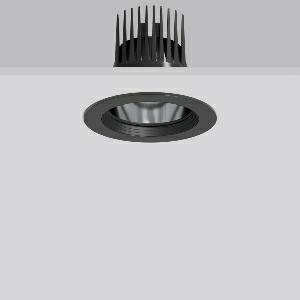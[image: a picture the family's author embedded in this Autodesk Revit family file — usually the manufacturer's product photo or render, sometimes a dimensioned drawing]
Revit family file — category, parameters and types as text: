
# Revit family: heledon_maxi_e_901756_003_1_76_3207
name_source: partatom
category: Lighting Fixtures
units: mm (PartAtom-declared; Revit-internal decimal feet)

## family parameters
Cut with Voids When Loaded = No
Host = Face
Light Source = No
Part Type = Normal
Room Calculation Point = No
Round Connector Dimension = Use Diameter
Shared = No

## types (1)
- HELEDON maxi E (1 x LED Modul 940, 3400 lm, 4000)
    Apparent Load = 25 VA
    Approval mark = CE
    CIE Flux Codes = 100 100 100 100 100
    Color Rendering = 92
    Color Temperature = 4000
    Default Elevation = 1800 mm
    Description = Series: HELEDON maxi
Round recessed downlight. Housing: die-cast aluminium, powder-coated. Black plastic ring and recessed LED to prevent glare from the side. Optical assembly with reflector made of MIRO-Silver with 98% total light reflection for outstanding efficiency - can be changed without tools. Best colour rendering index Ra>90. Suitable for Recessed ceiling mounting. Installation without tools thanks to spring fastening system. Including separate LED converter with connecting cable 600 mm.High quality converter without flickering and stroboscopic effect. Through-wiring box (5 pole) available as accessory. The following accessories can be mounted without use of tools: interchangeable lenses, decorative glasses, honeycomb louvre, clear and frosted diffusers, white interchangeable plastic ring. 
Colour: deep black, matt (RAL 9005)
Diameter: 162 mm
Height: 3 mm
Cut-out diameter: 152 mm
Recess height: 200 mm
Luminaire: recess height: 135 mm
Lamp: LED
Socket: without socket
Colour temperature: 4000K
Colour rendering index (CRI): 92
System power: 25 W
Rated luminous flux: 3400 lm
Luminous efficiency: 136 lm/W
Control gear: Converter, dimmable, DALI
Protection class: II
Type of protection: IP 20
    Height = 0 mm  [stored 0 ft]
    Lamp = 1 x LED Modul 940
    Lamp Light Flux = 3400 lm
    Lamp count = 1
    Length = 162 mm
    Lifetime = 50000 h
    Luminous efficacy = 136 lm/W
    Manufacturer = RZB
    ModVariant = No
    Model = 901756.003.1.76
    Mounting Place = Ceiling
    Mounting Type = Recessed
    Number of Poles = 1
    OnlyDefault = Yes
    Power Factor = 1
    Product Name = HELEDON maxi E
    Product group = Recessed downlights
    ProductGroupID = 402
    Protection Class = Protection class II
    Protection Degree = IP 20
    RLX_Detail_Level = 1
    RLX_Emergency_Light_Flux = 0 lm
    RLX_Emergency_Type = 0
    RLX_Emergency_Type_DB = No
    RlxData = <blob elided: 122805 chars, md5=a21ce109>
    Socket = socket
    Standby Power = 0 W
    System Light Flux = 3400 lm
    System Power = 25 W
    Type Comments = Product without accessories
    Type Image = 901662.003.jpg
    URL = http://relux.com
    VarID = ---
    Voltage = 230 V
    Voltage Range = 220-240 V
    Weight = 0.00 kg
    Width = 0 mm  [stored 0 ft]

note: [stored X ft] marks values corroborated as IEEE doubles in the binary element streams (Revit-internal decimal feet)

## geometry (parser evidence)
native form markers: Blend x4, Sweep x12
no freeform markers — native parametric forms only
